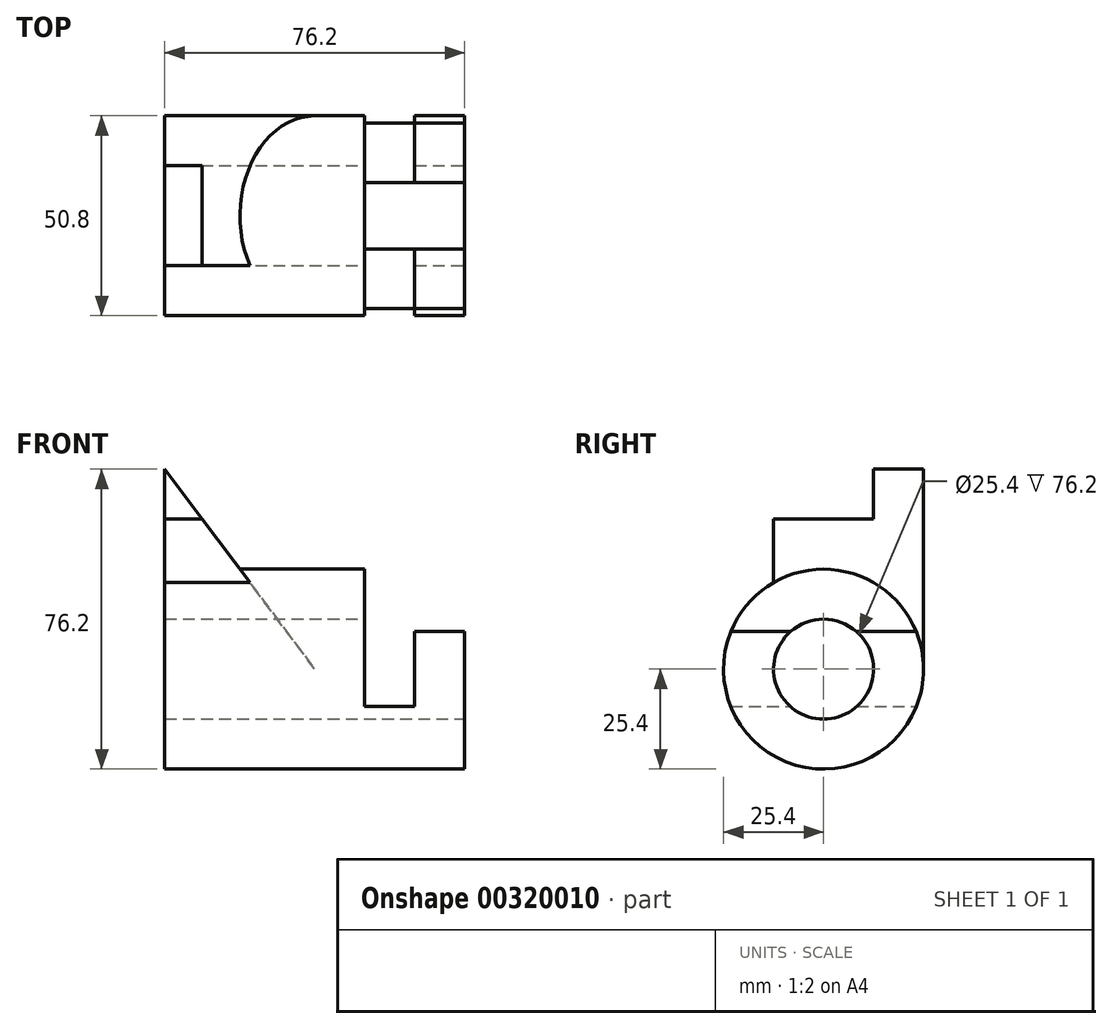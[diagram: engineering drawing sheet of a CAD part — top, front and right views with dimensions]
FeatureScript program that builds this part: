
annotation { "Feature Type Name" : "Feature", "Feature Type Description" : "" }
export const myFeature = defineFeature(function(context is Context, id is Id, definition is map)
    precondition{}
    {
        {
            var Q0;
            Q0=qCreatedBy(makeId("Right.planeOp"),FACE);
            var sketch = newSketch(context, id + "F0", { "sketchPlane" : qUnion([Q0])});
            skCircle(sketch, "E0", {"center": v(0, 0) * mm, "radius": 25.4 * mm});
            skCircle(sketch, "E1", {"center": v(0, 0) * mm, "radius": 12.7 * mm});
            skSolve(sketch);
        }
        {
            var Q0;
            Q0 = qSketchRegion(id + "F0", true);
            extrude(context, id + "F1", {"entities" : qUnion([Q0]), "oppositeDirection" : true, "depth" : 50.8 * mm});
        }
        {
            var Q0;
            Q0=makeQuery(id+"F1.opExtrude","CAP_FACE",FACE,{"disambiguationData":[OSD([sQuery(id+"F0.wireOp",EDGE,"E0"),sQuery(id+"F0.wireOp",EDGE,"E1")])],"isStart":true});
            var sketch = newSketch(context, id + "F2", { "sketchPlane" : qUnion([Q0])});
            skLineSegment(sketch, "E2", {"start": v(-23.55, -9.53) * mm, "end": v(-8.4, -9.53) * mm});
            skLineSegment(sketch, "E3", {"start": v(8.4, -9.53) * mm, "end": v(23.55, -9.53) * mm});
            skArc(sketch, "E4", {"start": v(-8.4, -9.53) * mm, "mid": v(0, -12.7) * mm, "end": v(8.4, -9.53) * mm});
            skArc(sketch, "E5", {"start": v(-23.55, -9.53) * mm, "mid": v(0, -25.4) * mm, "end": v(23.55, -9.53) * mm});
            skSolve(sketch);
        }
        {
            var Q0;
            Q0 = qSketchRegion(id + "F2", true);
            extrude(context, id + "F3", {"entities" : qUnion([Q0]), "operationType" : NewBodyOperationType.ADD, "depth" : 12.7 * mm});
        }
        {
            var Q0;
            Q0=makeQuery(id+"F3.opExtrude","CAP_FACE",FACE,{"disambiguationData":[OSD([sQuery(id+"F2.wireOp",EDGE,"E2"),sQuery(id+"F2.wireOp",EDGE,"E3"),sQuery(id+"F2.wireOp",EDGE,"E4"),sQuery(id+"F2.wireOp",EDGE,"E5")])],"isStart":false});
            var sketch = newSketch(context, id + "F4", { "sketchPlane" : qUnion([Q0])});
            skArc(sketch, "E6", {"start": v(-23.55, 9.52) * mm, "mid": v(0, -25.4) * mm, "end": v(23.55, 9.53) * mm});
            skArc(sketch, "E7", {"start": v(-8.4, 9.53) * mm, "mid": v(0, -12.7) * mm, "end": v(8.4, 9.52) * mm});
            skLineSegment(sketch, "E8", {"start": v(-23.55, 9.53) * mm, "end": v(-8.4, 9.53) * mm});
            skLineSegment(sketch, "E9", {"start": v(8.4, 9.53) * mm, "end": v(23.55, 9.53) * mm});
            skSolve(sketch);
        }
        {
            var Q0;
            {var subQ2=sQuery(id+"F4.wireOp",EDGE,"E8");Q0=makeQuery(id+"F4.imprint","IMPRINT",FACE,{"disambiguationData":[TD([[makeQuery(id+"F4.imprint","IMPRINT",EDGE,{"derivedFrom":subQ2}),-1.0]])]});}
            var Q1;
            {var subQ2=sQuery(id+"F4.wireOp",EDGE,"E9");Q1=makeQuery(id+"F4.imprint","IMPRINT",FACE,{"disambiguationData":[TD([[makeQuery(id+"F4.imprint","IMPRINT",EDGE,{"derivedFrom":subQ2}),-1.0]])]});}
            var Q2;
            {var subQ1=makeQuery(id+"F3.opExtrude","CAP_EDGE",EDGE,{"disambiguationData":[OSD([sQuery(id+"F2.wireOp",EDGE,"E2")])],"isStart":false});Q2=makeQuery(id+"F4.imprint","IMPRINT",FACE,{"disambiguationData":[TD([[makeQuery(id+"F4.imprint","IMPRINT",EDGE,{"derivedFrom":subQ1}),-1.0]])]});}
            extrude(context, id + "F5", {"entities" : qUnion([Q0, Q1, Q2]), "operationType" : NewBodyOperationType.ADD, "depth" : 12.7 * mm});
        }
        {
            var Q0;
            Q0=qCreatedBy(makeId("Front.planeOp"),FACE);
            cPlane(context, id + "F6", {"entities" : qUnion([Q0]), "cplaneType" : CPlaneType.OFFSET, "offset" : 6.35 * mm, "oppositeDirection" : true, "width" : 152.4 * mm, "height" : 152.4 * mm});
        }
        {
            var Q0;
            Q0=qCreatedBy(id+"F6.planeOp",FACE);
            var sketch = newSketch(context, id + "F7", { "sketchPlane" : qUnion([Q0])});
            skLineSegment(sketch, "E10", {"start": v(-12.7, 0) * mm, "end": v(-50.8, 50.8) * mm});
            skLineSegment(sketch, "E11", {"start": v(-50.8, 50.8) * mm, "end": v(-50.8, 0) * mm});
            skLineSegment(sketch, "E12", {"start": v(-12.7, 0) * mm, "end": v(-50.8, 0) * mm});
            skSolve(sketch);
        }
        {
            var Q0;
            Q0 = qSketchRegion(id + "F7", true);
            extrude(context, id + "F8", {"entities" : qUnion([Q0]), "operationType" : NewBodyOperationType.ADD, "endBound" : BoundingType.SYMMETRIC, "depth" : 38.1 * mm});
        }
        {
            var Q0;
            Q0=makeQuery(id+"F8.boolean.opBoolean","MERGE",FACE,{"derivedFrom":[makeQuery(id+"F1.opExtrude","CAP_FACE",FACE,{"disambiguationData":[OSD([sQuery(id+"F0.wireOp",EDGE,"E0"),sQuery(id+"F0.wireOp",EDGE,"E1")])],"isStart":false}),makeQuery(id+"F8.opExtrude","SWEPT_FACE",FACE,{"disambiguationData":[OSD([sQuery(id+"F7.wireOp",EDGE,"E11")])]})]});
            var sketch = newSketch(context, id + "F9", { "sketchPlane" : qUnion([Q0])});
            skCircle(sketch, "E13", {"center": v(0, 0) * mm, "radius": 12.7 * mm});
            skSolve(sketch);
        }
        {
            var Q0;
            Q0 = qSketchRegion(id + "F9", true);
            extrude(context, id + "F10", {"entities" : qUnion([Q0]), "operationType" : NewBodyOperationType.REMOVE, "oppositeDirection" : true, "depth" : 76.2 * mm});
        }
        {
            var Q0;
            Q0=qCreatedBy(makeId("Right.planeOp"),FACE);
            var sketch = newSketch(context, id + "F11", { "sketchPlane" : qUnion([Q0])});
            skLineSegment(sketch, "E14.bottom", {"start": v(-12.7, 38.1) * mm, "end": v(12.7, 38.1) * mm});
            skLineSegment(sketch, "E14.top", {"start": v(-12.7, 50.8) * mm, "end": v(12.7, 50.8) * mm});
            skLineSegment(sketch, "E14.left", {"start": v(-12.7, 38.1) * mm, "end": v(-12.7, 50.8) * mm});
            skLineSegment(sketch, "E14.right", {"start": v(12.7, 38.1) * mm, "end": v(12.7, 50.8) * mm});
            skSolve(sketch);
        }
        {
            var Q0;
            Q0 = qSketchRegion(id + "F11", true);
            extrude(context, id + "F12", {"entities" : qUnion([Q0]), "operationType" : NewBodyOperationType.REMOVE, "oppositeDirection" : true, "depth" : 50.8 * mm});
        }
    });
